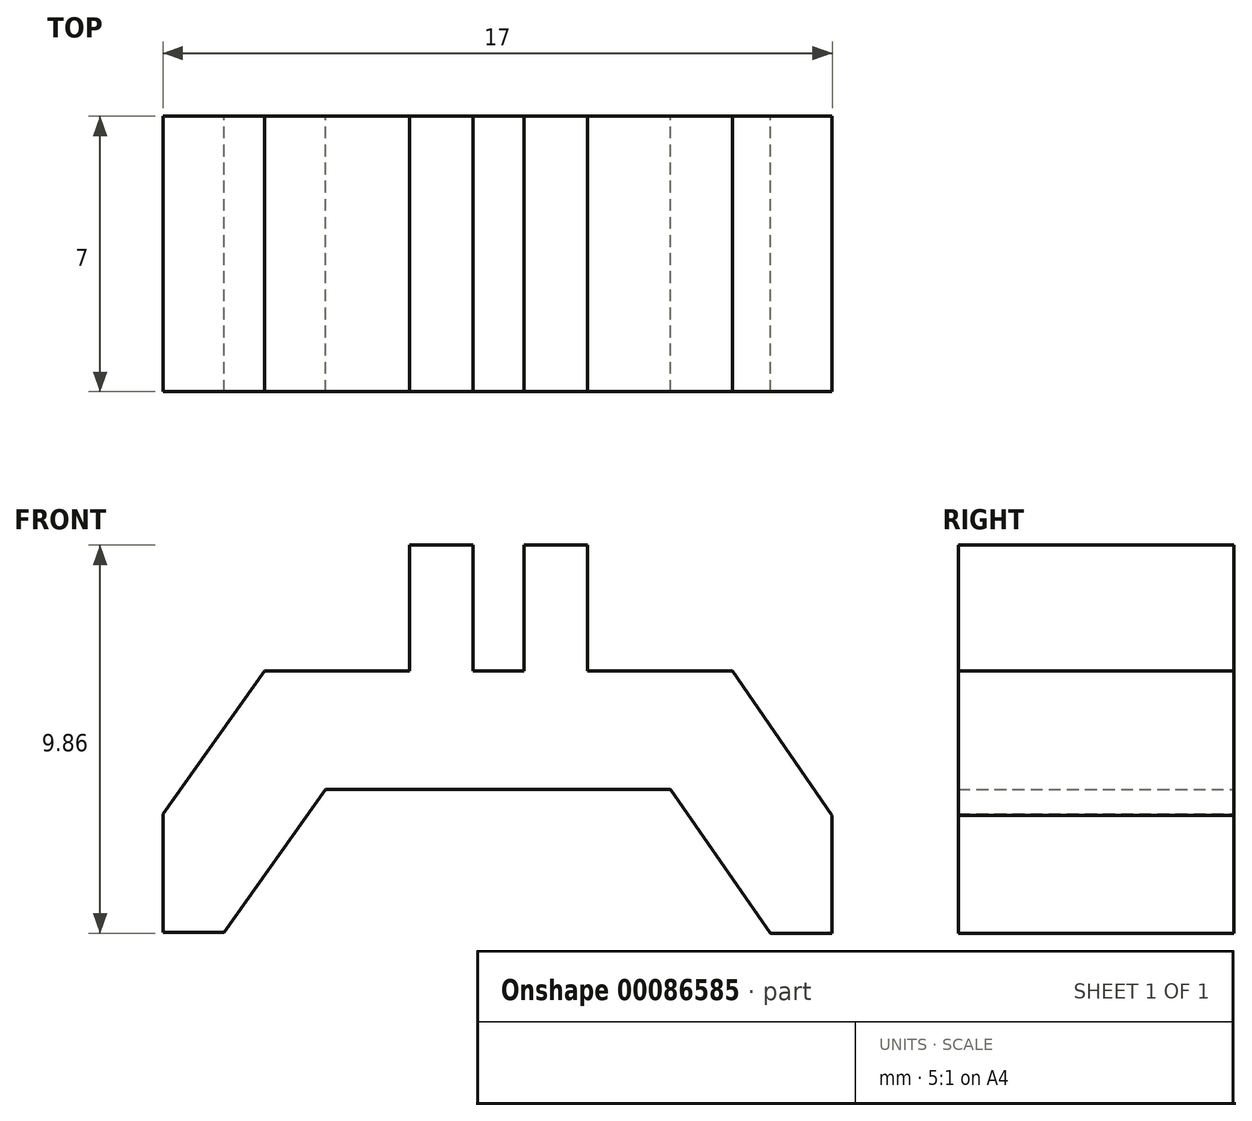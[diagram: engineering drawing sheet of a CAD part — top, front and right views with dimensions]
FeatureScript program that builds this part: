
annotation { "Feature Type Name" : "Feature", "Feature Type Description" : "" }
export const myFeature = defineFeature(function(context is Context, id is Id, definition is map)
    precondition{}
    {
        {
            var Q0;
            Q0=qCreatedBy(makeId("Front.planeOp"),FACE);
            var sketch = newSketch(context, id + "F0", { "sketchPlane" : qUnion([Q0])});
            skLineSegment(sketch, "E0.bottom", {"start": v(-17.7, 12.68) * mm, "end": v(-16.08, 12.68) * mm});
            skLineSegment(sketch, "E0.top", {"start": v(-17.7, 9.48) * mm, "end": v(-16.08, 9.48) * mm});
            skLineSegment(sketch, "E0.left", {"start": v(-17.7, 12.68) * mm, "end": v(-17.7, 9.48) * mm});
            skLineSegment(sketch, "E0.right", {"start": v(-16.08, 12.68) * mm, "end": v(-16.08, 9.48) * mm});
            skLineSegment(sketch, "E1.bottom", {"start": v(-19, 9.48) * mm, "end": v(-20.6, 9.48) * mm});
            skLineSegment(sketch, "E1.top", {"start": v(-19, 12.68) * mm, "end": v(-20.6, 12.68) * mm});
            skLineSegment(sketch, "E1.left", {"start": v(-19, 9.48) * mm, "end": v(-19, 12.68) * mm});
            skLineSegment(sketch, "E1.right", {"start": v(-20.6, 9.48) * mm, "end": v(-20.6, 12.68) * mm});
            skLineSegment(sketch, "E2", {"start": v(-24.28, 9.48) * mm, "end": v(-12.4, 9.48) * mm});
            skLineSegment(sketch, "E3", {"start": v(-24.28, 9.48) * mm, "end": v(-26.86, 5.85) * mm});
            skLineSegment(sketch, "E4", {"start": v(-12.4, 9.48) * mm, "end": v(-9.86, 5.82) * mm});
            skLineSegment(sketch, "E5.2", {"start": v(-13.97, 6.48) * mm, "end": v(-11.43, 2.82) * mm});
            skLineSegment(sketch, "E5.3", {"start": v(-22.73, 6.48) * mm, "end": v(-13.97, 6.48) * mm});
            skLineSegment(sketch, "E5.4", {"start": v(-22.73, 6.48) * mm, "end": v(-25.32, 2.85) * mm});
            skLineSegment(sketch, "E6", {"start": v(-26.86, 5.85) * mm, "end": v(-26.86, 2.85) * mm});
            skLineSegment(sketch, "E7", {"start": v(-26.86, 2.85) * mm, "end": v(-25.32, 2.85) * mm});
            skLineSegment(sketch, "E8", {"start": v(-9.86, 5.82) * mm, "end": v(-9.86, 2.82) * mm});
            skLineSegment(sketch, "E9", {"start": v(-9.86, 2.82) * mm, "end": v(-11.43, 2.82) * mm});
            skSolve(sketch);
        }
        {
            var Q0;
            Q0 = qSketchRegion(id + "F0", true);
            extrude(context, id + "F1", {"entities" : qUnion([Q0]), "depth" : 7 * mm});
        }
    });
